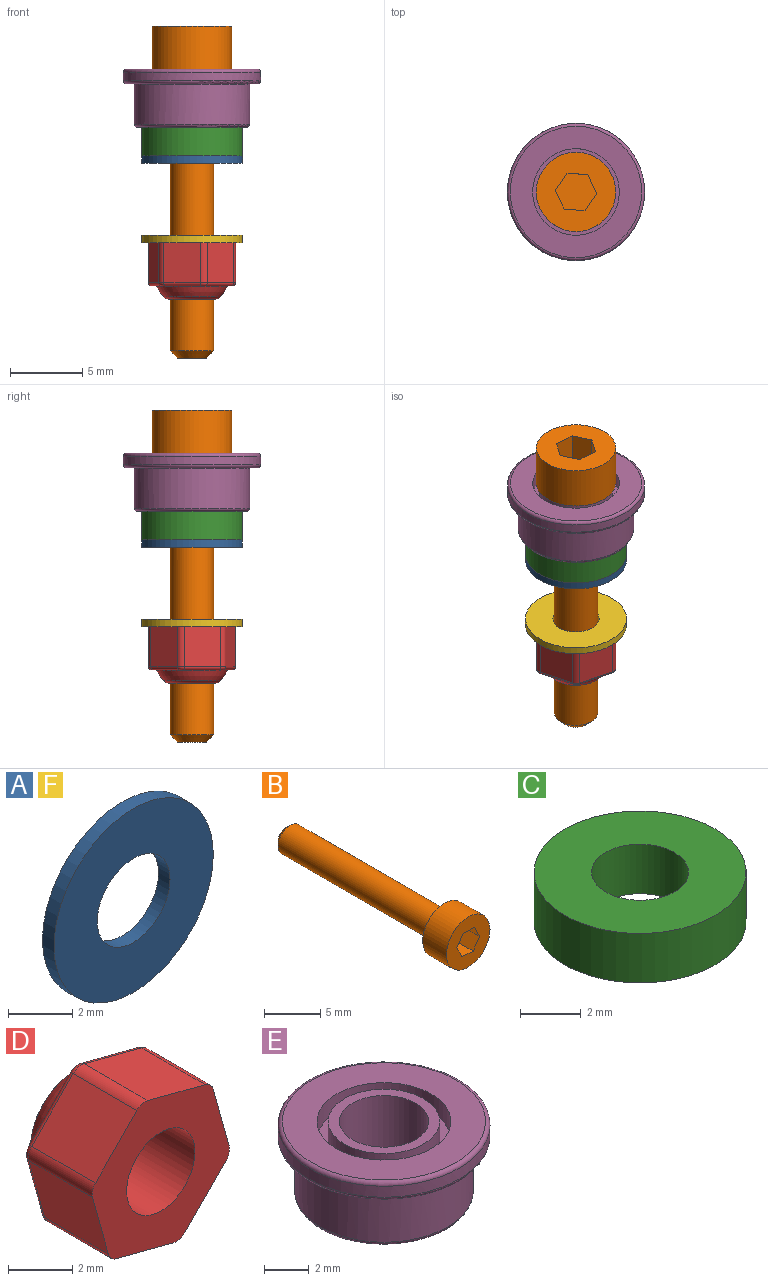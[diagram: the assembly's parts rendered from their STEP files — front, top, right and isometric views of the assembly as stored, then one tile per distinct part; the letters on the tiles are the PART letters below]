
ASSEMBLY  parts=6 mates=5
PART A: 4 faces, bbox 7x0.5x7 mm
  f0: cylinder r=1.6mm len=3.2mm, axis (0,1,0), area 5mm2, adj f2,f3
  f1: cylinder r=3.5mm len=7mm, axis (0,1,0), area 11mm2, adj f2,f3
  f2: plane 7x7mm, normal (0,-1,0), area 30.4mm2, adj f0,f1
  f3: plane 7x7mm, normal (0,1,0), area 30.4mm2, adj f0,f1
PART B: 13 faces, bbox 5.5x23x5.5 mm
  f0: plane 5.5x5.5mm, normal (0,-1,0), area 18.3mm2, adj f1,f5,f6,f7,f8,f9,f10
  f1: cylinder r=2.75mm len=5.5mm, axis (0,1,0), area 51.8mm2, adj f0,f2
  f2: plane 5.5x5.5mm, normal (0,1,0), area 16.7mm2, adj f1,f3
  f3: cylinder r=1.5mm len=19.5mm, axis (0,-1,0), area 183.8mm2, adj f2,f12
  f4: plane 2x2mm, normal (0,1,0), area 3.1mm2, adj f12
  f5: plane 2.5x1.3mm, normal (0.9,0,0.43), area 3.6mm2, adj f0,f6,f10,f11
  f6: plane 2.5x1.44mm, normal (0.08,0,1), area 3.6mm2, adj f0,f5,f7,f11
  f7: plane 2.5x1.19mm, normal (-0.83,0,0.56), area 3.6mm2, adj f0,f6,f8,f11
  f8: plane 2.5x1.3mm, normal (-0.9,0,-0.43), area 3.6mm2, adj f0,f7,f9,f11
  f9: plane 2.5x1.44mm, normal (-0.08,0,-1), area 3.6mm2, adj f0,f8,f10,f11
  f10: plane 2.5x1.19mm, normal (0.83,0,-0.56), area 3.6mm2, adj f0,f5,f9,f11
  f11: plane 2.88x2.6mm, normal (0,-1,0), area 5.4mm2, adj f5,f6,f7,f8,f9,f10
  f12: cone r=1mm half-angle=45deg, axis (0,-1,0), area 5.6mm2, adj f3,f4
PART C: 4 faces, bbox 7x7x2 mm
  f0: cylinder r=1.6mm len=3.2mm, axis (0,0,-1), area 20.1mm2, adj f2,f3
  f1: cylinder r=3.5mm len=7mm, axis (0,0,-1), area 44mm2, adj f2,f3
  f2: plane 7x7mm, normal (0,0,1), area 30.4mm2, adj f0,f1
  f3: plane 7x7mm, normal (0,0,-1), area 30.4mm2, adj f0,f1
PART D: 31 faces, bbox 6.1x3.9x6.1 mm
  f0: sphere r=2.68mm, area 11.8mm2, adj f2,f11
  f1: plane 3.2x3.2mm, normal (0,1,0), area 0.9mm2, adj f2,f12
  f2: torus R=1.6mm, axis (0,-1,0), area 4.6mm2, adj f0,f1
  f3: plane 2.8x2.5mm, normal (0.96,0,0.27), area 7.3mm2, adj f9,f13,f18,f29
  f4: plane 2.8x2.52mm, normal (0.25,0,0.97), area 7.3mm2, adj f9,f13,f14,f28
  f5: plane 2.8x1.85mm, normal (-0.71,0,0.7), area 7.3mm2, adj f9,f14,f15,f24
  f6: plane 2.8x2.5mm, normal (-0.96,0,-0.27), area 7.3mm2, adj f9,f15,f16,f20
  f7: plane 2.8x2.52mm, normal (-0.25,0,-0.97), area 7.3mm2, adj f9,f16,f17,f21
  f8: plane 2.8x1.85mm, normal (0.71,0,-0.7), area 7.3mm2, adj f9,f17,f18,f25
  f9: plane 6.03x6.01mm, normal (0,-1,0), area 19mm2, adj f3,f4,f5,f6,f7,f8,f12,f13
  f10: plane 5.63x5.61mm, normal (0,1,0), area 2.5mm2, adj f11,f19,f20,f21,f22,f23,f24,f25
  f11: torus R=2.52mm, axis (0,-1,0), area 1.8mm2, adj f0,f10
  f12: cylinder r=1.5mm len=3.92mm, axis (0,1,0), area 36.9mm2, adj f1,f9
  f13: cylinder r=0.5mm len=2.8mm, axis (0,1,0), area 1.5mm2, adj f3,f4,f9,f30
  f14: cylinder r=0.5mm len=2.8mm, axis (0,1,0), area 1.5mm2, adj f4,f5,f9,f26
  f15: cylinder r=0.5mm len=2.8mm, axis (0,1,0), area 1.5mm2, adj f5,f6,f9,f22
  f16: cylinder r=0.5mm len=2.8mm, axis (0,1,0), area 1.5mm2, adj f6,f7,f9,f19
  f17: cylinder r=0.5mm len=2.8mm, axis (0,1,0), area 1.5mm2, adj f7,f8,f9,f23
  f18: cylinder r=0.5mm len=2.8mm, axis (0,1,0), area 1.5mm2, adj f3,f8,f9,f27
  f19: torus R=0.3mm, axis (0,-1,0), area 0.1mm2, adj f10,f16,f20,f21
  f20: cylinder r=0.2mm len=2.56mm, axis (0.27,0,-0.96), area 0.8mm2, adj f6,f10,f19,f22
  f21: cylinder r=0.2mm len=2.57mm, axis (0.97,0,-0.25), area 0.8mm2, adj f7,f10,f19,f23
  f22: torus R=0.3mm, axis (0,-1,0), area 0.1mm2, adj f10,f15,f20,f24
  f23: torus R=0.3mm, axis (0,-1,0), area 0.1mm2, adj f10,f17,f21,f25
  f24: cylinder r=0.2mm len=1.99mm, axis (-0.7,0,-0.71), area 0.8mm2, adj f5,f10,f22,f26
  f25: cylinder r=0.2mm len=1.99mm, axis (0.7,0,0.71), area 0.8mm2, adj f8,f10,f23,f27
  f26: torus R=0.3mm, axis (0,-1,0), area 0.1mm2, adj f10,f14,f24,f28
  f27: torus R=0.3mm, axis (0,-1,0), area 0.1mm2, adj f10,f18,f25,f29
  f28: cylinder r=0.2mm len=2.57mm, axis (-0.97,0,0.25), area 0.8mm2, adj f4,f10,f26,f30
  f29: cylinder r=0.2mm len=2.56mm, axis (-0.27,0,0.96), area 0.8mm2, adj f3,f10,f27,f30
  f30: torus R=0.3mm, axis (0,-1,0), area 0.1mm2, adj f10,f13,f28,f29
PART E: 18 faces, bbox 10.3x10.3x4 mm
  f0: plane 5x5mm, normal (0,0,-1), area 7.1mm2, adj f1,f14
  f1: cylinder r=2.5mm len=5mm, axis (0,0,-1), area 15.7mm2, adj f0,f2
  f2: plane 6x6mm, normal (0,0,-1), area 8.6mm2, adj f1,f3
  f3: cylinder r=3mm len=6mm, axis (0,0,-1), area 18.8mm2, adj f2,f4
  f4: plane 7.6x7.6mm, normal (0,0,-1), area 17.1mm2, adj f3,f15
  f5: cylinder r=4mm len=8mm, axis (0,0,-1), area 69.1mm2, adj f6,f15
  f6: torus R=4mm, axis (0,0,-1), area 5.9mm2, adj f5,f7
  f7: plane 9.1x9.1mm, normal (0,0,-1), area 13.5mm2, adj f6,f16
  f8: cylinder r=4.75mm len=9.5mm, axis (0,0,-1), area 17.9mm2, adj f16,f17
  f9: plane 9.1x9.1mm, normal (0,0,1), area 36.8mm2, adj f10,f17
  f10: cylinder r=3mm len=6mm, axis (0,0,-1), area 18.8mm2, adj f9,f11
  f11: plane 6x6mm, normal (0,0,1), area 8.6mm2, adj f10,f12
  f12: cylinder r=2.5mm len=5mm, axis (0,0,-1), area 15.7mm2, adj f11,f13
  f13: plane 5x5mm, normal (0,0,1), area 7.1mm2, adj f12,f14
  f14: cylinder r=2mm len=4mm, axis (0,0,-1), area 50.3mm2, adj f0,f13
  f15: torus R=3.8mm, axis (0,0,1), area 7.8mm2, adj f4,f5
  f16: torus R=4.55mm, axis (0,0,1), area 9.2mm2, adj f7,f8
  f17: torus R=4.55mm, axis (0,0,-1), area 9.2mm2, adj f8,f9
PART F: same geometry as A
PLACE A rot(axis=(1,0,0),90deg) t=(-2.66,0.12,-1.52)mm
PLACE B rot(axis=(-1,0,0),90deg) t=(-2.66,0.12,4.48)mm
PLACE C rot(axis=(1,0,0),180deg) t=(-2.66,0.12,0.48)mm
PLACE D rot(axis=(-1,0,0),90deg) t=(-2.66,0.12,-10.52)mm
PLACE E t=(-2.66,0.12,0.48)mm fixed
PLACE F rot(axis=(-1,0,0),90deg) t=(-2.66,0.12,-7.52)mm
MATE revolute C.f0 <-> E.f1  axis (0,0,1) through (-2.66,0.12,0.48)mm
MATE revolute B.f1 <-> E.f1  axis (0,0,1) through (-2.66,0.12,4.48)mm
MATE revolute F.f0 <-> A.f0  axis (0,0,1) through (-2.66,0.12,-7.02)mm
MATE revolute D.f2 <-> F.f0  axis (0,0,1) through (-2.66,0.12,-7.52)mm
MATE revolute C.f0 <-> A.f0  axis (0,0,-1) through (-2.66,0.12,-1.52)mm
